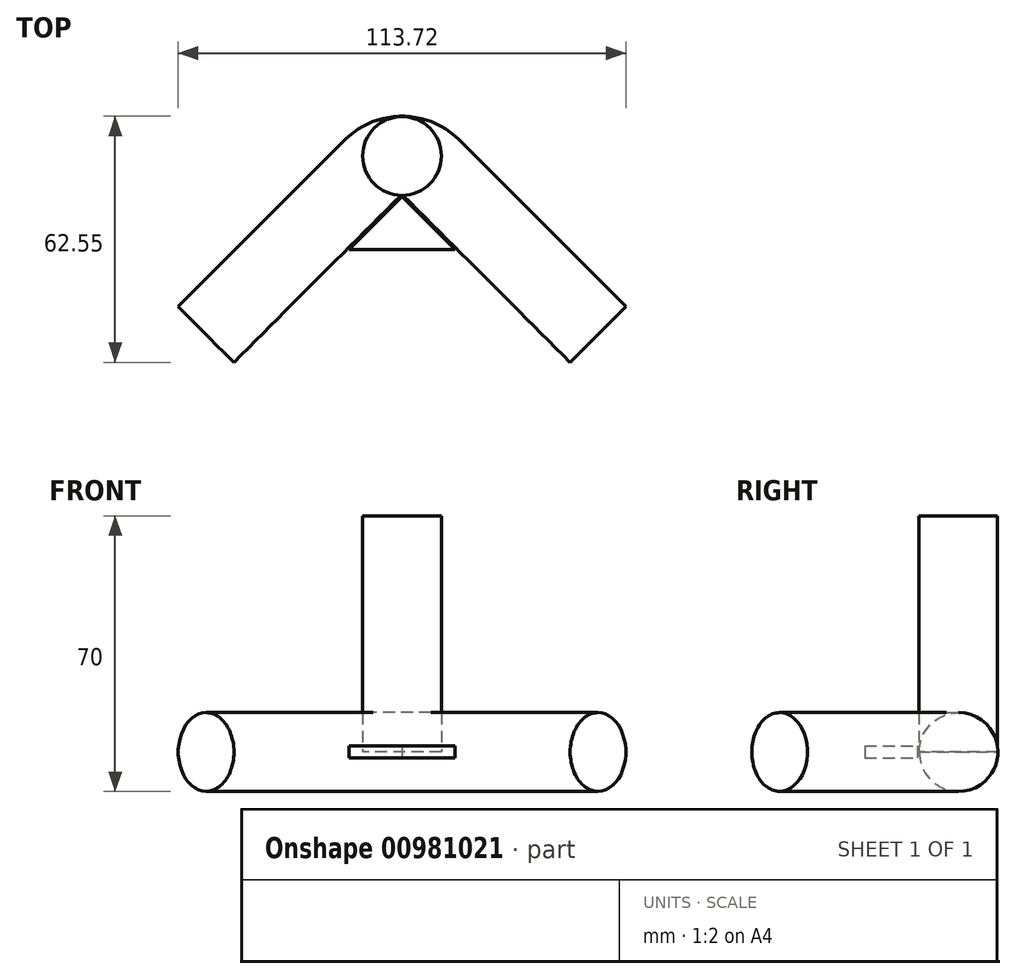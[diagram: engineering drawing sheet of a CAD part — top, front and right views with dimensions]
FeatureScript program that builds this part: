
annotation { "Feature Type Name" : "Feature", "Feature Type Description" : "" }
export const myFeature = defineFeature(function(context is Context, id is Id, definition is map)
    precondition{}
    {
        {
            var Q0;
            Q0=qCreatedBy(makeId("Top.planeOp"),FACE);
            var sketch = newSketch(context, id + "F0", { "sketchPlane" : qUnion([Q0])});
            skArc(sketch, "E0", {"start": v(7.07, 7.07) * mm, "mid": v(0, 10) * mm, "end": v(-7.07, 7.07) * mm});
            skLineSegment(sketch, "E1", {"start": v(-7.07, 7.07) * mm, "end": v(-49.5, -35.36) * mm});
            skLineSegment(sketch, "E2.MirrorCS", {"start": v(7.07, 7.07) * mm, "end": v(49.5, -35.36) * mm});
            skLineSegment(sketch, "E3", {"start": v(0, 0) * mm, "end": v(-13.44, -13.44) * mm});
            skLineSegment(sketch, "E4", {"start": v(-13.44, -13.44) * mm, "end": v(13.44, -13.44) * mm});
            skLineSegment(sketch, "E5", {"start": v(13.44, -13.44) * mm, "end": v(0, 0) * mm});
            skSolve(sketch);
        }
        {
            var Q0;
            Q0=sQuery(id+"F0.wireOp",VERTEX,"E1.end");
            var Q1;
            Q1=sQuery(id+"F0.wireOp",EDGE,"E1");
            cPlane(context, id + "F1", {"entities" : qUnion([Q0, Q1]), "cplaneType" : CPlaneType.CURVE_POINT, "offset" : 25 * mm, "width" : 150 * mm, "height" : 150 * mm});
        }
        {
            var Q0;
            Q0=qCreatedBy(id+"F1.planeOp",FACE);
            var sketch = newSketch(context, id + "F2", { "sketchPlane" : qUnion([Q0])});
            skCircle(sketch, "E6", {"center": v(-10.4, 0) * mm, "radius": 10 * mm});
            skSolve(sketch);
        }
        {
            var Q0;
            Q0=qCreatedBy(makeId("Front.planeOp"),FACE);
            cPlane(context, id + "F3", {"entities" : qUnion([Q0]), "cplaneType" : CPlaneType.OFFSET, "offset" : 10 * mm, "oppositeDirection" : true, "width" : 150 * mm, "height" : 150 * mm});
        }
        {
            var Q0;
            Q0=qCreatedBy(id+"F3.planeOp",FACE);
            var sketch = newSketch(context, id + "F4", { "sketchPlane" : qUnion([Q0])});
            skLineSegment(sketch, "E7", {"start": v(0, 0) * mm, "end": v(0, 60) * mm});
            skPoint(sketch, "E8", {"position": v(0, 60) * mm});
            skLineSegment(sketch, "E9", {"start": v(0, 0) * mm, "end": v(0, 103.03) * mm, "construction": true});
            skSolve(sketch);
        }
        {
            var Q0;
            Q0=qCreatedBy(makeId("Top.planeOp"),FACE);
            cPlane(context, id + "F5", {"entities" : qUnion([Q0]), "cplaneType" : CPlaneType.OFFSET, "offset" : 60 * mm, "width" : 150 * mm, "height" : 150 * mm});
        }
        {
            var Q0;
            Q0=qCreatedBy(id+"F5.planeOp",FACE);
            var sketch = newSketch(context, id + "F6", { "sketchPlane" : qUnion([Q0])});
            skCircle(sketch, "E10", {"center": v(0, 10.3) * mm, "radius": 10 * mm});
            skSolve(sketch);
        }
        {
            var Q0;
            Q0=makeQuery(id+"F6.imprint","IMPRINT",FACE,{"disambiguationData":[TD([[makeQuery(id+"F6.imprint","IMPRINT",EDGE,{"derivedFrom":sQuery(id+"F6.wireOp",EDGE,"E10")}),1.0]])]});
            var Q1;
            Q1=sQuery(id+"F4.wireOp",EDGE,"E7");
            sweep(context, id + "F7", {"profiles" : qUnion([Q0]), "path" : qUnion([Q1])});
        }
        {
            var Q0;
            Q0=makeQuery(id+"F2.imprint","IMPRINT",FACE,{"disambiguationData":[TD([[makeQuery(id+"F2.imprint","IMPRINT",EDGE,{"derivedFrom":sQuery(id+"F2.wireOp",EDGE,"E6")}),1.0]])]});
            var Q1;
            Q1=sQuery(id+"F0.wireOp",EDGE,"E1");
            var Q2;
            Q2=sQuery(id+"F0.wireOp",EDGE,"E0");
            var Q3;
            Q3=sQuery(id+"F0.wireOp",EDGE,"E2.MirrorCS");
            sweep(context, id + "F8", {"profiles" : qUnion([Q0]), "path" : qUnion([Q1, Q2, Q3])});
        }
        {
            var Q0;
            Q0 = qSketchRegion(id + "F0", true);
            extrude(context, id + "F9", {"entities" : qUnion([Q0]), "endBound" : BoundingType.SYMMETRIC, "depth" : 3 * mm, "offsetDistance" : 25 * mm});
        }
    });
